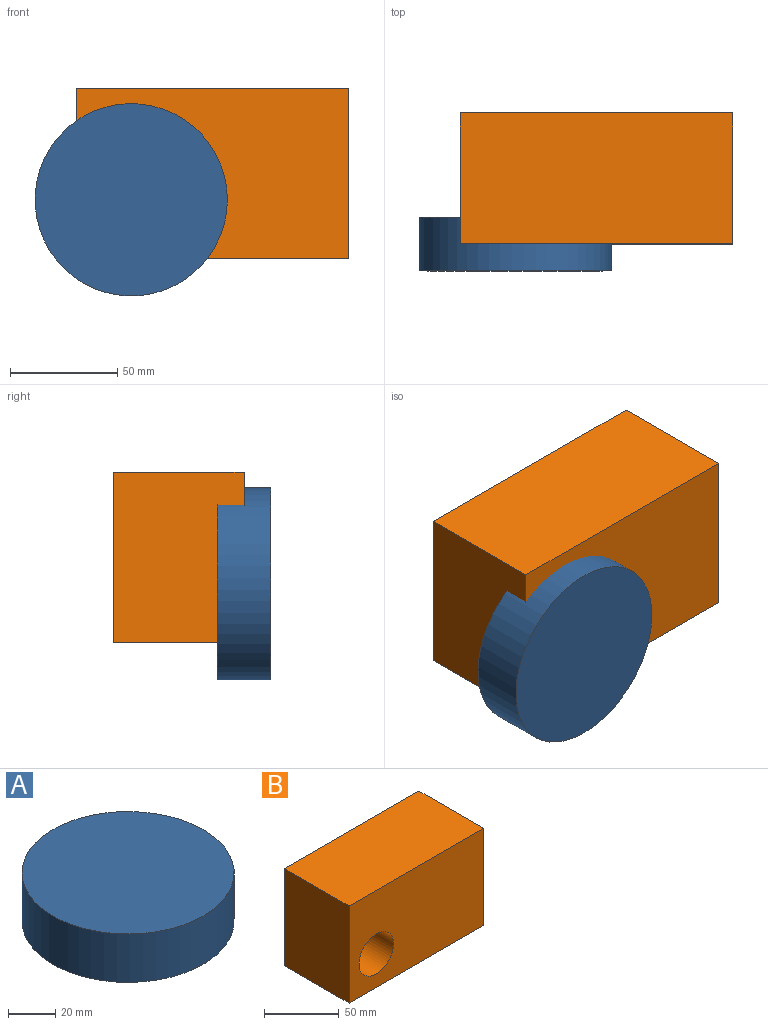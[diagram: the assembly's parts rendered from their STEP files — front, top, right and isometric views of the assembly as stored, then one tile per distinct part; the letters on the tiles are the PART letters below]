
ASSEMBLY  parts=2 mates=1
PART A: 3 faces, bbox 89.5x89.5x25 mm
  f0: cylinder r=44.77mm len=89.54mm, axis (0,0,-1), area 7032.6mm2, adj f1,f2
  f1: plane 89.54x89.54mm, normal (0,0,1), area 6297.1mm2, adj f0
  f2: plane 89.54x89.54mm, normal (0,0,-1), area 6297.1mm2, adj f0
PART B: 8 faces, bbox 127x61x79.3 mm
  f0: plane 79.32x61mm, normal (-1,0,0), area 4838.4mm2, adj f1,f3,f4,f5
  f1: plane 127x61mm, normal (0,0,-1), area 7747mm2, adj f0,f2,f4,f5
  f2: plane 79.32x61mm, normal (1,0,0), area 4838.4mm2, adj f1,f3,f4,f5
  f3: plane 127x61mm, normal (0,0,1), area 7747mm2, adj f0,f2,f4,f5
  f4: plane 127x79.32mm, normal (0,-1,0), area 9237.8mm2, adj f0,f1,f2,f3,f6
  f5: plane 127x79.32mm, normal (0,1,0), area 10073.3mm2, adj f0,f1,f2,f3
  f6: cylinder r=16.31mm len=32.62mm, axis (0,-1,0), area 2561.7mm2, adj f4,f7
  f7: plane 32.62x32.62mm, normal (0,-1,0), area 835.5mm2, adj f6
PLACE A rot(axis=(-1,0,0),90deg) t=(-63.64,-85.67,-27.45)mm
PLACE B t=(-40.33,-12.17,-13.04)mm
MATE planar A.f0 <-> B.f6  axis (0,-1,0) through (-63.64,-73.17,-27.45)mm
